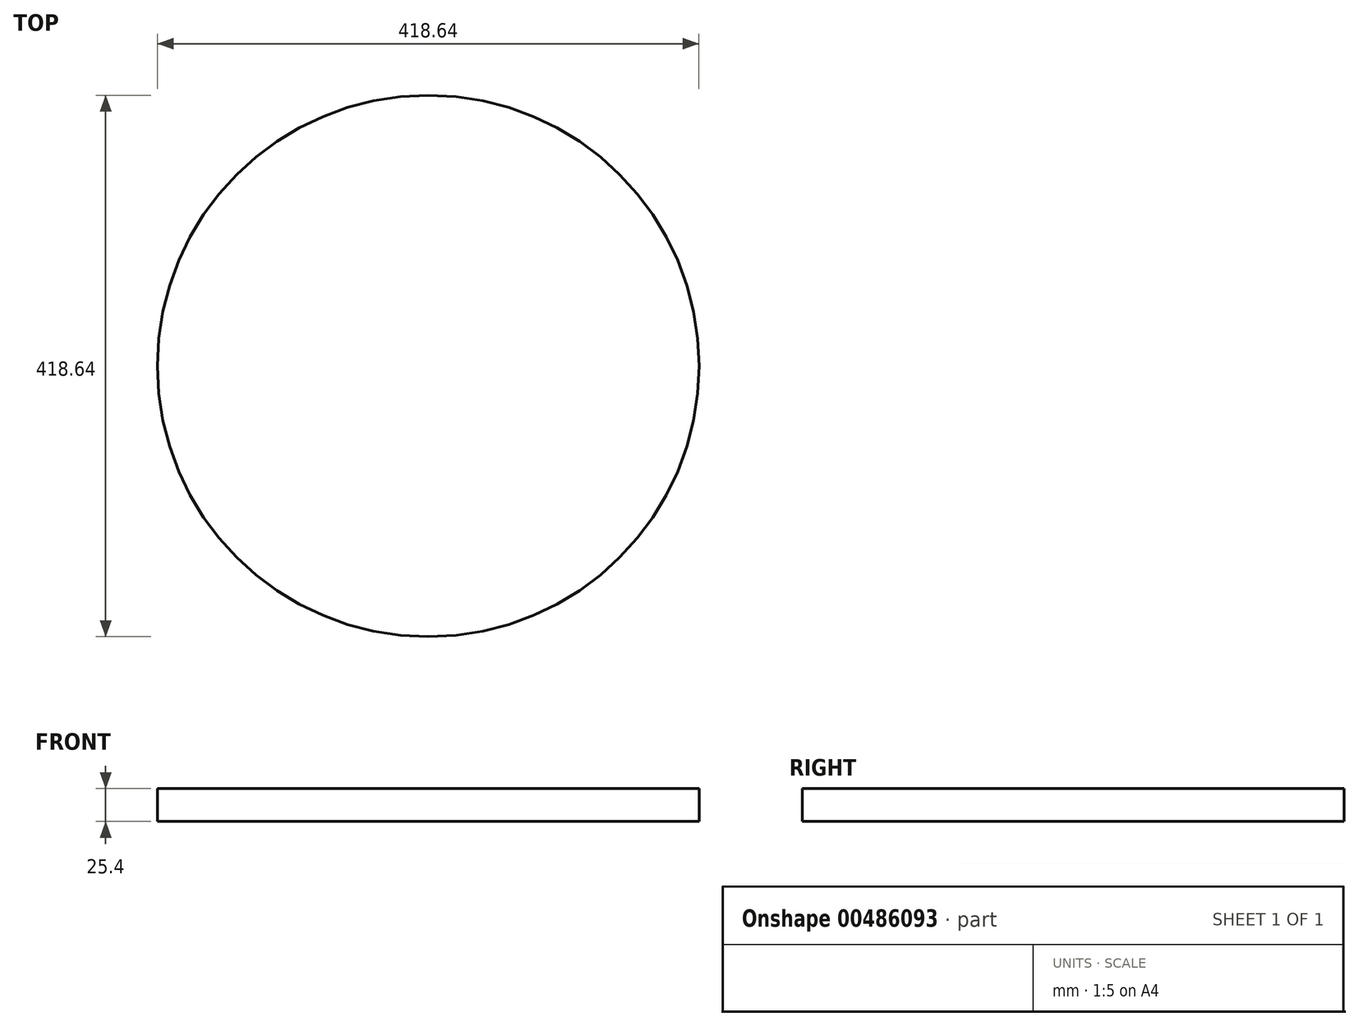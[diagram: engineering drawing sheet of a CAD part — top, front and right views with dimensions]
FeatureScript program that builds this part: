
annotation { "Feature Type Name" : "Feature", "Feature Type Description" : "" }
export const myFeature = defineFeature(function(context is Context, id is Id, definition is map)
    precondition{}
    {
        {
            var Q0;
            Q0=qCreatedBy(makeId("Top.planeOp"),FACE);
            var sketch = newSketch(context, id + "F0", { "sketchPlane" : qUnion([Q0])});
            skCircle(sketch, "E0", {"center": v(0, 0) * mm, "radius": 209.32 * mm});
            skSolve(sketch);
        }
        {
            var Q0;
            Q0=makeQuery(id+"F0.imprint","IMPRINT",FACE,{"disambiguationData":[TD([[makeQuery(id+"F0.imprint","IMPRINT",EDGE,{"derivedFrom":sQuery(id+"F0.wireOp",EDGE,"E0")}),1.0]])]});
            extrude(context, id + "F1", {"entities" : qUnion([Q0]), "depth" : 25.4 * mm});
        }
    });
